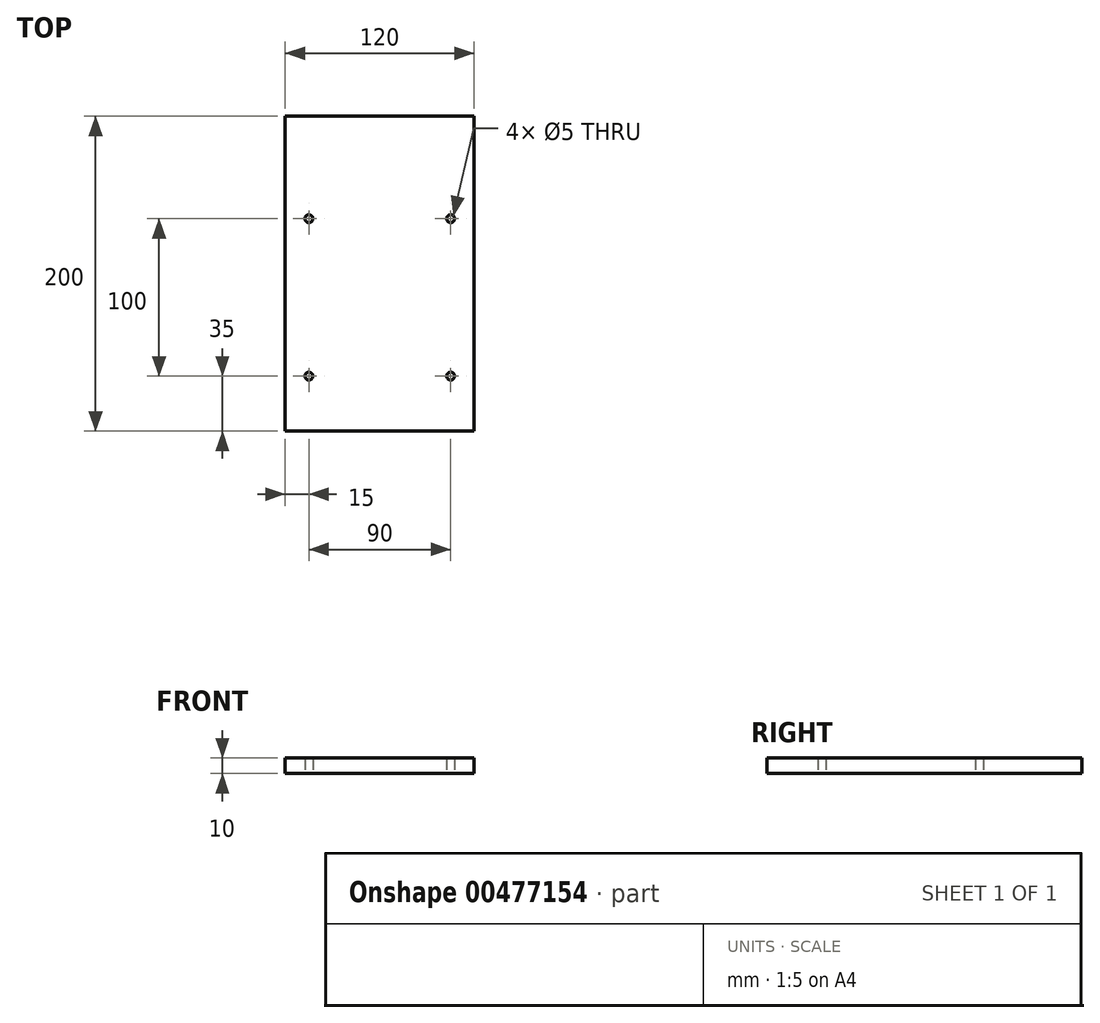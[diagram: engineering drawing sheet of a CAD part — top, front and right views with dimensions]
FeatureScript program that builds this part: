
annotation { "Feature Type Name" : "Feature", "Feature Type Description" : "" }
export const myFeature = defineFeature(function(context is Context, id is Id, definition is map)
    precondition{}
    {
        {
            var Q0;
            Q0=qCreatedBy(makeId("Top.planeOp"),FACE);
            var sketch = newSketch(context, id + "F0", { "sketchPlane" : qUnion([Q0])});
            skLineSegment(sketch, "E0.bottom", {"start": v(-60, 65) * mm, "end": v(60, 65) * mm});
            skLineSegment(sketch, "E0.top", {"start": v(-60, -135) * mm, "end": v(60, -135) * mm});
            skLineSegment(sketch, "E0.left", {"start": v(-60, 65) * mm, "end": v(-60, -135) * mm});
            skLineSegment(sketch, "E0.right", {"start": v(60, 65) * mm, "end": v(60, -135) * mm});
            skCircle(sketch, "E1", {"center": v(-45, -100) * mm, "radius": 2.5 * mm});
            skCircle(sketch, "E2", {"center": v(45, -100) * mm, "radius": 2.5 * mm});
            skPoint(sketch, "E3", {"position": v(-45, 0) * mm});
            skPoint(sketch, "E4", {"position": v(45, 0) * mm});
            skCircle(sketch, "E5", {"center": v(-45, 0) * mm, "radius": 2.5 * mm});
            skCircle(sketch, "E6", {"center": v(45, 0) * mm, "radius": 2.5 * mm});
            skSolve(sketch);
        }
        {
            var Q0;
            Q0=qSketchRegion(id+"F0",true);
            extrude(context, id + "F1", {"entities" : qUnion([Q0]), "depth" : 10 * mm});
        }
    });
